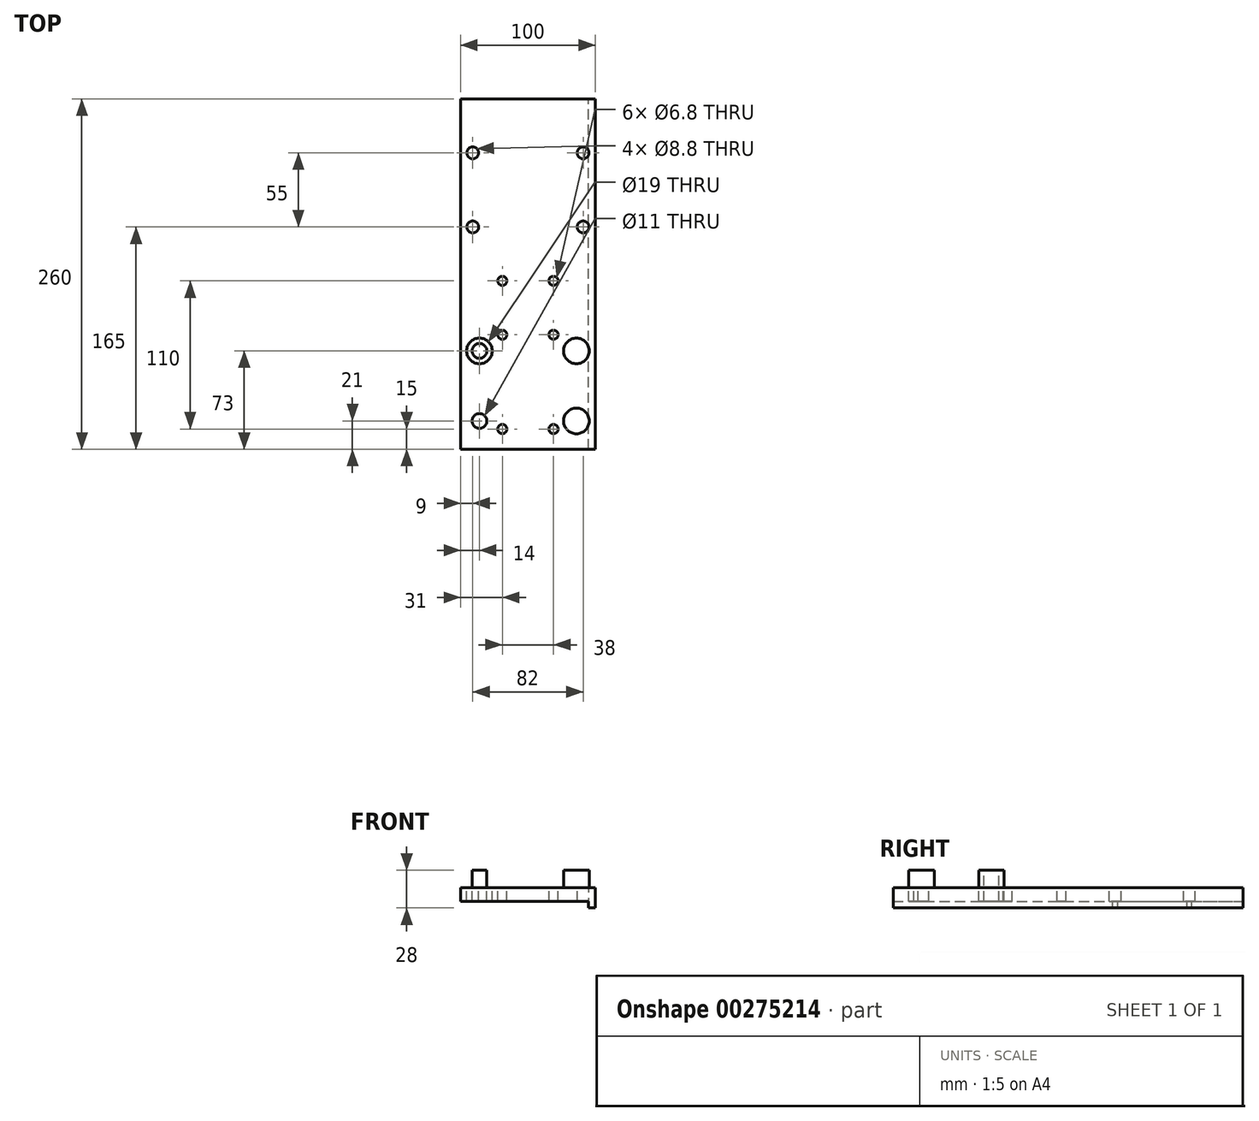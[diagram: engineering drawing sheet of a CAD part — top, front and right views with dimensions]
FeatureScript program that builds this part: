
annotation { "Feature Type Name" : "Feature", "Feature Type Description" : "" }
export const myFeature = defineFeature(function(context is Context, id is Id, definition is map)
    precondition{}
    {
        {
            var Q0;
            Q0=qCreatedBy(makeId("Front.planeOp"),FACE);
            var sketch = newSketch(context, id + "F0", { "sketchPlane" : qUnion([Q0])});
            skLineSegment(sketch, "E0", {"start": v(-50, 0) * mm, "end": v(45, 0) * mm});
            skLineSegment(sketch, "E1", {"start": v(45, 0) * mm, "end": v(45, -5) * mm});
            skLineSegment(sketch, "E2", {"start": v(45, -5) * mm, "end": v(50, -5) * mm});
            skLineSegment(sketch, "E3", {"start": v(50, -5) * mm, "end": v(50, 23) * mm});
            skLineSegment(sketch, "E4", {"start": v(50, 23) * mm, "end": v(-50, 23) * mm});
            skLineSegment(sketch, "E5", {"start": v(-50, 23) * mm, "end": v(-50, 0) * mm});
            skSolve(sketch);
        }
        {
            var Q0;
            Q0=makeQuery(id+"F0.imprint","IMPRINT",FACE,{"disambiguationData":[TD([[makeQuery(id+"F0.imprint","IMPRINT",EDGE,{"derivedFrom":sQuery(id+"F0.wireOp",EDGE,"E0")}),1.0]])]});
            extrude(context, id + "F1", {"entities" : qUnion([Q0]), "endBound" : BoundingType.SYMMETRIC, "depth" : 260 * mm});
        }
        {
            var Q0;
            Q0=makeQuery(id+"F1.opExtrude","SWEPT_FACE",FACE,{"disambiguationData":[OSD([sQuery(id+"F0.wireOp",EDGE,"E4")])]});
            var sketch = newSketch(context, id + "F2", { "sketchPlane" : qUnion([Q0])});
            skCircle(sketch, "E6", {"center": v(-36, -109) * mm, "radius": 9.5 * mm});
            skCircle(sketch, "E7", {"center": v(-36, -109) * mm, "radius": 5.5 * mm});
            skLineSegment(sketch, "E8", {"start": v(-88.02, -83) * mm, "end": v(96.42, -83) * mm, "construction": true});
            skCircle(sketch, "E9.MirrorC", {"center": v(36, -109) * mm, "radius": 9.5 * mm});
            skCircle(sketch, "E10.MirrorC", {"center": v(36, -109) * mm, "radius": 5.5 * mm});
            skCircle(sketch, "E11.MirrorC", {"center": v(-36, -57) * mm, "radius": 9.5 * mm});
            skCircle(sketch, "E12.MirrorC", {"center": v(-36, -57) * mm, "radius": 5.5 * mm});
            skCircle(sketch, "E13.MirrorC", {"center": v(36, -57) * mm, "radius": 9.5 * mm});
            skCircle(sketch, "E14.MirrorC", {"center": v(36, -57) * mm, "radius": 5.5 * mm});
            skSolve(sketch);
        }
        {
            var Q0;
            Q0=makeQuery(id+"F2.imprint","IMPRINT",FACE,{"disambiguationData":[TD([[makeQuery(id+"F2.imprint","IMPRINT",EDGE,{"derivedFrom":sQuery(id+"F2.wireOp",EDGE,"E7")}),1.0]])]});
            var Q1;
            Q1=makeQuery(id+"F2.imprint","IMPRINT",FACE,{"disambiguationData":[TD([[makeQuery(id+"F2.imprint","IMPRINT",EDGE,{"derivedFrom":sQuery(id+"F2.wireOp",EDGE,"E12.MirrorC")}),-1.0]])]});
            extrude(context, id + "F3", {"entities" : qUnion([Q0, Q1]), "operationType" : NewBodyOperationType.REMOVE, "oppositeDirection" : true, "depth" : 25 * mm});
        }
        {
            var Q0;
            Q0=makeQuery(id+"F2.imprint","IMPRINT",FACE,{"disambiguationData":[TD([[makeQuery(id+"F2.imprint","IMPRINT",EDGE,{"derivedFrom":sQuery(id+"F2.wireOp",EDGE,"E6")}),1.0]])]});
            var Q1;
            Q1=makeQuery(id+"F2.imprint","IMPRINT",FACE,{"disambiguationData":[TD([[makeQuery(id+"F2.imprint","IMPRINT",EDGE,{"derivedFrom":sQuery(id+"F2.wireOp",EDGE,"E11.MirrorC")}),-1.0]])]});
            extrude(context, id + "F4", {"entities" : qUnion([Q0, Q1]), "operationType" : NewBodyOperationType.REMOVE, "oppositeDirection" : true, "depth" : 13 * mm});
        }
        {
            var Q0;
            Q0=makeQuery(id+"F1.opExtrude","SWEPT_FACE",FACE,{"disambiguationData":[OSD([sQuery(id+"F0.wireOp",EDGE,"E4")])]});
            var sketch = newSketch(context, id + "F5", { "sketchPlane" : qUnion([Q0])});
            skPoint(sketch, "E15", {"position": v(-19, -115) * mm});
            skPoint(sketch, "E16.MirrorP", {"position": v(19, -115) * mm});
            skLineSegment(sketch, "E17", {"start": v(-93.77, -80) * mm, "end": v(95.86, -80) * mm, "construction": true});
            skPoint(sketch, "E18.MirrorP", {"position": v(-19, -45) * mm});
            skPoint(sketch, "E19.MirrorP", {"position": v(19, -45) * mm});
            skLineSegment(sketch, "E20", {"start": v(-92.5, -25) * mm, "end": v(124.64, -25) * mm, "construction": true});
            skPoint(sketch, "E21.MirrorP", {"position": v(19, -5) * mm});
            skPoint(sketch, "E22.MirrorP", {"position": v(-19, -5) * mm});
            skPoint(sketch, "E23", {"position": v(-41, 35) * mm});
            skPoint(sketch, "E24.MirrorP", {"position": v(41, 35) * mm});
            skLineSegment(sketch, "E25", {"start": v(-112.7, 62.5) * mm, "end": v(157.38, 62.5) * mm, "construction": true});
            skPoint(sketch, "E26.MirrorP", {"position": v(-41, 90) * mm});
            skPoint(sketch, "E27.MirrorP", {"position": v(41, 90) * mm});
            skSolve(sketch);
        }
        {
            var Q0;
            Q0=sQuery(id+"F5.wireOp",VERTEX,"E15");
            var Q1;
            Q1=sQuery(id+"F5.wireOp",VERTEX,"E16.MirrorP");
            var Q2;
            Q2=sQuery(id+"F5.wireOp",VERTEX,"E18.MirrorP");
            var Q3;
            Q3=sQuery(id+"F5.wireOp",VERTEX,"E19.MirrorP");
            var Q4;
            Q4=sQuery(id+"F5.wireOp",VERTEX,"E21.MirrorP");
            var Q5;
            Q5=sQuery(id+"F5.wireOp",VERTEX,"E22.MirrorP");
            var Q6;
            Q6=makeQuery(id+"F1.opExtrude","SWEPT_BODY",BODY,{"disambiguationData":[OSD([sQuery(id+"F0.wireOp",EDGE,"E0"),sQuery(id+"F0.wireOp",EDGE,"E1"),sQuery(id+"F0.wireOp",EDGE,"E2"),sQuery(id+"F0.wireOp",EDGE,"E3"),sQuery(id+"F0.wireOp",EDGE,"E4"),sQuery(id+"F0.wireOp",EDGE,"E5")])]});
            hole(context, id + "F6", {"style" : HoleStyle.SIMPLE, "endStyle" : HoleEndStyle.THROUGH, "standardTappedOrClearance" : lookupTablePath({ "standard" : "ISO", "engagement" : "75%", "pitch" : "1.25 mm", "size" : "M8", "type" : "Tapped" }), "standardBlindInLast" : lookupTablePath({ "standard" : "ISO", "engagement" : "75%", "pitch" : "1.25 mm", "size" : "M8", "type" : "Tapped" }), "holeDiameter" : 6.8 * mm, "showTappedDepth" : true, "tappedDepth" : 12 * mm, "tapClearance" : 3, "locations" : qUnion([Q0, Q1, Q2, Q3, Q4, Q5]), "scope" : qUnion([Q6]), "majorDiameter" : 8 * mm});
        }
        {
            var Q0;
            Q0=sQuery(id+"F5.wireOp",VERTEX,"E23");
            var Q1;
            Q1=sQuery(id+"F5.wireOp",VERTEX,"E24.MirrorP");
            var Q2;
            Q2=sQuery(id+"F5.wireOp",VERTEX,"E27.MirrorP");
            var Q3;
            Q3=sQuery(id+"F5.wireOp",VERTEX,"E26.MirrorP");
            var Q4;
            Q4=makeQuery(id+"F1.opExtrude","SWEPT_BODY",BODY,{"disambiguationData":[OSD([sQuery(id+"F0.wireOp",EDGE,"E0"),sQuery(id+"F0.wireOp",EDGE,"E1"),sQuery(id+"F0.wireOp",EDGE,"E2"),sQuery(id+"F0.wireOp",EDGE,"E3"),sQuery(id+"F0.wireOp",EDGE,"E4"),sQuery(id+"F0.wireOp",EDGE,"E5")])]});
            hole(context, id + "F7", {"style" : HoleStyle.SIMPLE, "endStyle" : HoleEndStyle.THROUGH, "standardTappedOrClearance" : lookupTablePath({ "standard" : "ISO", "engagement" : "75%", "pitch" : "1.25 mm", "size" : "M10", "type" : "Tapped" }), "standardBlindInLast" : lookupTablePath({ "standard" : "ISO", "engagement" : "75%", "pitch" : "1.25 mm", "size" : "M10", "type" : "Tapped" }), "holeDiameter" : 8.8 * mm, "showTappedDepth" : true, "tappedDepth" : 12 * mm, "tapClearance" : 3, "locations" : qUnion([Q0, Q1, Q2, Q3]), "scope" : qUnion([Q4]), "majorDiameter" : 10 * mm});
        }
    });
